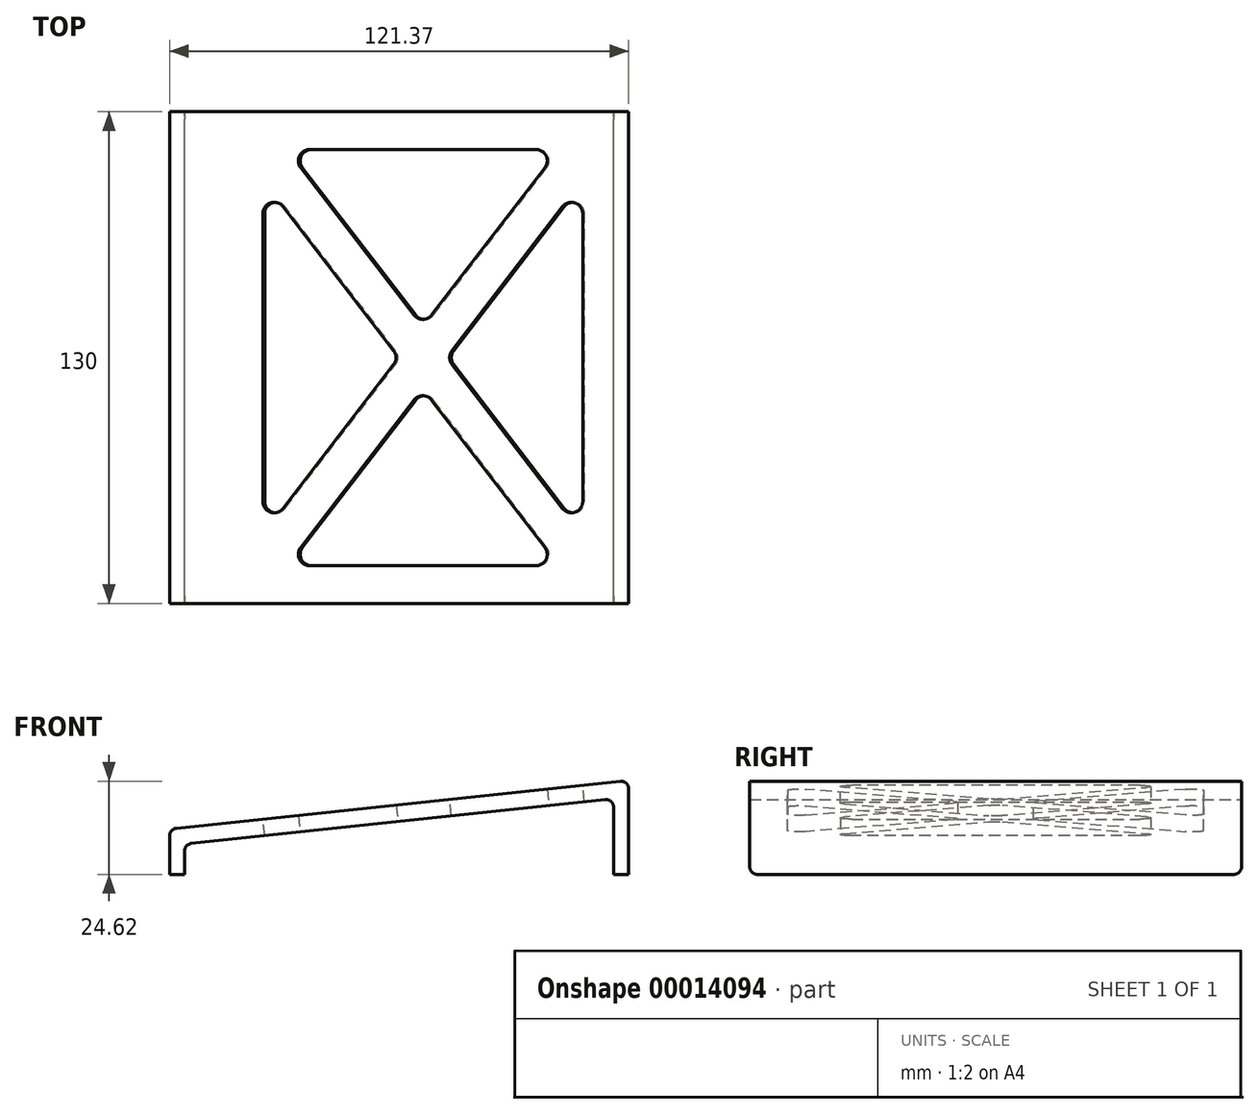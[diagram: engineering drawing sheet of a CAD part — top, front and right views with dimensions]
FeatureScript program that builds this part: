
annotation { "Feature Type Name" : "Feature", "Feature Type Description" : "" }
export const myFeature = defineFeature(function(context is Context, id is Id, definition is map)
    precondition{}
    {
        {
            var Q0;
            Q0=qCreatedBy(makeId("Front.planeOp"),FACE);
            var sketch = newSketch(context, id + "F0", { "sketchPlane" : qUnion([Q0])});
            skLineSegment(sketch, "E0", {"start": v(0, 0) * mm, "end": v(0, 8) * mm});
            skLineSegment(sketch, "E1", {"start": v(113.37, 0) * mm, "end": v(113.37, 20) * mm});
            skLineSegment(sketch, "E2", {"start": v(0, 8) * mm, "end": v(113.37, 20) * mm});
            skLineSegment(sketch, "E3", {"start": v(0, 0) * mm, "end": v(-4, 0) * mm});
            skLineSegment(sketch, "E4", {"start": v(-4, 0) * mm, "end": v(-4, 12) * mm});
            skLineSegment(sketch, "E5", {"start": v(-4, 12) * mm, "end": v(117.37, 24.85) * mm});
            skLineSegment(sketch, "E6", {"start": v(117.37, 24.85) * mm, "end": v(117.37, 0) * mm});
            skLineSegment(sketch, "E7", {"start": v(117.37, 0) * mm, "end": v(113.37, 0) * mm});
            skSolve(sketch);
        }
        {
            var Q0;
            Q0 = qSketchRegion(id + "F0", true);
            extrude(context, id + "F1", {"entities" : qUnion([Q0]), "depth" : 130 * mm});
        }
        {
            var Q0;
            Q0=makeQuery(id+"F1.opExtrude","SWEPT_EDGE",EDGE,{"disambiguationData":[OSD([sQuery(id+"F0.wireOp",EDGE,"E4"),sQuery(id+"F0.wireOp",EDGE,"E5")])]});
            var Q1;
            Q1=makeQuery(id+"F1.opExtrude","SWEPT_EDGE",EDGE,{"disambiguationData":[OSD([sQuery(id+"F0.wireOp",EDGE,"E5"),sQuery(id+"F0.wireOp",EDGE,"E6")])]});
            var Q2;
            Q2=makeQuery(id+"F1.opExtrude","SWEPT_EDGE",EDGE,{"disambiguationData":[OSD([sQuery(id+"F0.wireOp",EDGE,"E0"),sQuery(id+"F0.wireOp",EDGE,"E2")])]});
            var Q3;
            Q3=makeQuery(id+"F1.opExtrude","SWEPT_EDGE",EDGE,{"disambiguationData":[OSD([sQuery(id+"F0.wireOp",EDGE,"E1"),sQuery(id+"F0.wireOp",EDGE,"E2")])]});
            var Q4;
            Q4=makeQuery(id+"F1.opExtrude","CAP_EDGE",EDGE,{"disambiguationData":[OSD([sQuery(id+"F0.wireOp",EDGE,"E3")])],"isStart":false});
            var Q5;
            Q5=makeQuery(id+"F1.opExtrude","CAP_EDGE",EDGE,{"disambiguationData":[OSD([sQuery(id+"F0.wireOp",EDGE,"E3")])],"isStart":true});
            var Q6;
            Q6=makeQuery(id+"F1.opExtrude","CAP_EDGE",EDGE,{"disambiguationData":[OSD([sQuery(id+"F0.wireOp",EDGE,"E7")])],"isStart":true});
            var Q7;
            Q7=makeQuery(id+"F1.opExtrude","CAP_EDGE",EDGE,{"disambiguationData":[OSD([sQuery(id+"F0.wireOp",EDGE,"E7")])],"isStart":false});
            fillet(context, id + "F2", {"entities" : qUnion([Q0, Q1, Q2, Q3, Q4, Q5, Q6, Q7]), "radius" : 2 * mm, "tangentPropagation" : true, "allowEdgeOverflow" : false});
        }
        {
            var Q0;
            Q0=makeQuery(id+"F1.opExtrude","SWEPT_FACE",FACE,{"disambiguationData":[OSD([sQuery(id+"F0.wireOp",EDGE,"E5")])]});
            var sketch = newSketch(context, id + "F3", { "sketchPlane" : qUnion([Q0])});
            skLineSegment(sketch, "E8", {"start": v(117.1, -65) * mm, "end": v(-0.92, -65) * mm, "construction": true});
            skLineSegment(sketch, "E9", {"start": v(58.1, -65) * mm, "end": v(58.1, 0) * mm, "construction": true});
            skLineSegment(sketch, "E10", {"start": v(58.1, -65) * mm, "end": v(58.1, -130) * mm, "construction": true});
            skLineSegment(sketch, "E11", {"start": v(22.1, 0) * mm, "end": v(22.1, -130) * mm, "construction": true});
            skLineSegment(sketch, "E12", {"start": v(117.1, -10) * mm, "end": v(22.1, -10) * mm, "construction": true});
            skLineSegment(sketch, "E13.0.MirrorCS", {"start": v(117.1, -120) * mm, "end": v(22.1, -120) * mm, "construction": true});
            skLineSegment(sketch, "E14", {"start": v(107.1, 0) * mm, "end": v(107.1, -130) * mm, "construction": true});
            skLineSegment(sketch, "E15", {"start": v(22.1, -10) * mm, "end": v(107.1, -120) * mm, "construction": true});
            skLineSegment(sketch, "E16", {"start": v(107.1, -10) * mm, "end": v(22.1, -120) * mm, "construction": true});
            skLineSegment(sketch, "E17", {"start": v(28.43, -10) * mm, "end": v(107.1, -111.82) * mm});
            skLineSegment(sketch, "E18", {"start": v(22.1, -18.18) * mm, "end": v(100.79, -120) * mm});
            skLineSegment(sketch, "E19", {"start": v(100.79, -10) * mm, "end": v(22.1, -111.82) * mm});
            skLineSegment(sketch, "E20", {"start": v(28.43, -120) * mm, "end": v(107.1, -18.18) * mm});
            skLineSegment(sketch, "E21", {"start": v(100.79, -10) * mm, "end": v(28.43, -10) * mm});
            skLineSegment(sketch, "E22", {"start": v(107.1, -18.18) * mm, "end": v(107.1, -111.82) * mm});
            skLineSegment(sketch, "E23", {"start": v(100.79, -120) * mm, "end": v(28.43, -120) * mm});
            skLineSegment(sketch, "E24", {"start": v(22.1, -111.82) * mm, "end": v(22.1, -18.18) * mm});
            skSolve(sketch);
        }
        {
            var Q0;
            {var subQ0=sQuery(id+"F3.wireOp",EDGE,"E21");Q0=makeQuery(id+"F3.imprint","IMPRINT",FACE,{"disambiguationData":[TD([[makeQuery(id+"F3.imprint","IMPRINT",EDGE,{"derivedFrom":subQ0}),1.0]])]});}
            var Q1;
            {var subQ0=sQuery(id+"F3.wireOp",EDGE,"E22");Q1=makeQuery(id+"F3.imprint","IMPRINT",FACE,{"disambiguationData":[TD([[makeQuery(id+"F3.imprint","IMPRINT",EDGE,{"derivedFrom":subQ0}),-1.0]])]});}
            var Q2;
            {var subQ0=sQuery(id+"F3.wireOp",EDGE,"E23");Q2=makeQuery(id+"F3.imprint","IMPRINT",FACE,{"disambiguationData":[TD([[makeQuery(id+"F3.imprint","IMPRINT",EDGE,{"derivedFrom":subQ0}),-1.0]])]});}
            var Q3;
            {var subQ0=sQuery(id+"F3.wireOp",EDGE,"E24");Q3=makeQuery(id+"F3.imprint","IMPRINT",FACE,{"disambiguationData":[TD([[makeQuery(id+"F3.imprint","IMPRINT",EDGE,{"derivedFrom":subQ0}),-1.0]])]});}
            extrude(context, id + "F4", {"entities" : qUnion([Q0, Q1, Q2, Q3]), "operationType" : NewBodyOperationType.REMOVE, "endBound" : BoundingType.UP_TO_NEXT, "oppositeDirection" : true, "depth" : 25 * mm});
        }
        {
            var Q0;
            Q0=makeQuery(id+"F4.boolean.opBoolean","COPY",EDGE,{"derivedFrom":makeQuery(id+"F4.opExtrude","SWEPT_EDGE",EDGE,{"disambiguationData":[OSD([sQuery(id+"F3.wireOp",EDGE,"E19"),sQuery(id+"F3.wireOp",EDGE,"E21")])]})});
            var Q1;
            Q1=makeQuery(id+"F4.boolean.opBoolean","COPY",EDGE,{"derivedFrom":makeQuery(id+"F4.opExtrude","SWEPT_EDGE",EDGE,{"disambiguationData":[OSD([sQuery(id+"F3.wireOp",EDGE,"E17"),sQuery(id+"F3.wireOp",EDGE,"E19")])]})});
            var Q2;
            Q2=makeQuery(id+"F4.boolean.opBoolean","COPY",EDGE,{"derivedFrom":makeQuery(id+"F4.opExtrude","SWEPT_EDGE",EDGE,{"disambiguationData":[OSD([sQuery(id+"F3.wireOp",EDGE,"E18"),sQuery(id+"F3.wireOp",EDGE,"E19")])]})});
            var Q3;
            Q3=makeQuery(id+"F4.boolean.opBoolean","COPY",EDGE,{"derivedFrom":makeQuery(id+"F4.opExtrude","SWEPT_EDGE",EDGE,{"disambiguationData":[OSD([sQuery(id+"F3.wireOp",EDGE,"E18"),sQuery(id+"F3.wireOp",EDGE,"E24")])]})});
            var Q4;
            Q4=makeQuery(id+"F4.boolean.opBoolean","COPY",EDGE,{"derivedFrom":makeQuery(id+"F4.opExtrude","SWEPT_EDGE",EDGE,{"disambiguationData":[OSD([sQuery(id+"F3.wireOp",EDGE,"E17"),sQuery(id+"F3.wireOp",EDGE,"E21")])]})});
            var Q5;
            Q5=makeQuery(id+"F4.boolean.opBoolean","COPY",EDGE,{"derivedFrom":makeQuery(id+"F4.opExtrude","SWEPT_EDGE",EDGE,{"disambiguationData":[OSD([sQuery(id+"F3.wireOp",EDGE,"E20"),sQuery(id+"F3.wireOp",EDGE,"E22")])]})});
            var Q6;
            Q6=makeQuery(id+"F4.boolean.opBoolean","COPY",EDGE,{"derivedFrom":makeQuery(id+"F4.opExtrude","SWEPT_EDGE",EDGE,{"disambiguationData":[OSD([sQuery(id+"F3.wireOp",EDGE,"E17"),sQuery(id+"F3.wireOp",EDGE,"E20")])]})});
            var Q7;
            Q7=makeQuery(id+"F4.boolean.opBoolean","COPY",EDGE,{"derivedFrom":makeQuery(id+"F4.opExtrude","SWEPT_EDGE",EDGE,{"disambiguationData":[OSD([sQuery(id+"F3.wireOp",EDGE,"E20"),sQuery(id+"F3.wireOp",EDGE,"E23")])]})});
            var Q8;
            Q8=makeQuery(id+"F4.boolean.opBoolean","COPY",EDGE,{"derivedFrom":makeQuery(id+"F4.opExtrude","SWEPT_EDGE",EDGE,{"disambiguationData":[OSD([sQuery(id+"F3.wireOp",EDGE,"E19"),sQuery(id+"F3.wireOp",EDGE,"E24")])]})});
            var Q9;
            Q9=makeQuery(id+"F4.boolean.opBoolean","COPY",EDGE,{"derivedFrom":makeQuery(id+"F4.opExtrude","SWEPT_EDGE",EDGE,{"disambiguationData":[OSD([sQuery(id+"F3.wireOp",EDGE,"E18"),sQuery(id+"F3.wireOp",EDGE,"E23")])]})});
            var Q10;
            Q10=makeQuery(id+"F4.boolean.opBoolean","COPY",EDGE,{"derivedFrom":makeQuery(id+"F4.opExtrude","SWEPT_EDGE",EDGE,{"disambiguationData":[OSD([sQuery(id+"F3.wireOp",EDGE,"E18"),sQuery(id+"F3.wireOp",EDGE,"E20")])]})});
            var Q11;
            Q11=makeQuery(id+"F4.boolean.opBoolean","COPY",EDGE,{"derivedFrom":makeQuery(id+"F4.opExtrude","SWEPT_EDGE",EDGE,{"disambiguationData":[OSD([sQuery(id+"F3.wireOp",EDGE,"E17"),sQuery(id+"F3.wireOp",EDGE,"E22")])]})});
            fillet(context, id + "F5", {"entities" : qUnion([Q0, Q1, Q2, Q3, Q4, Q5, Q6, Q7, Q8, Q9, Q10, Q11]), "radius" : 3 * mm, "tangentPropagation" : true, "allowEdgeOverflow" : false});
        }
    });
